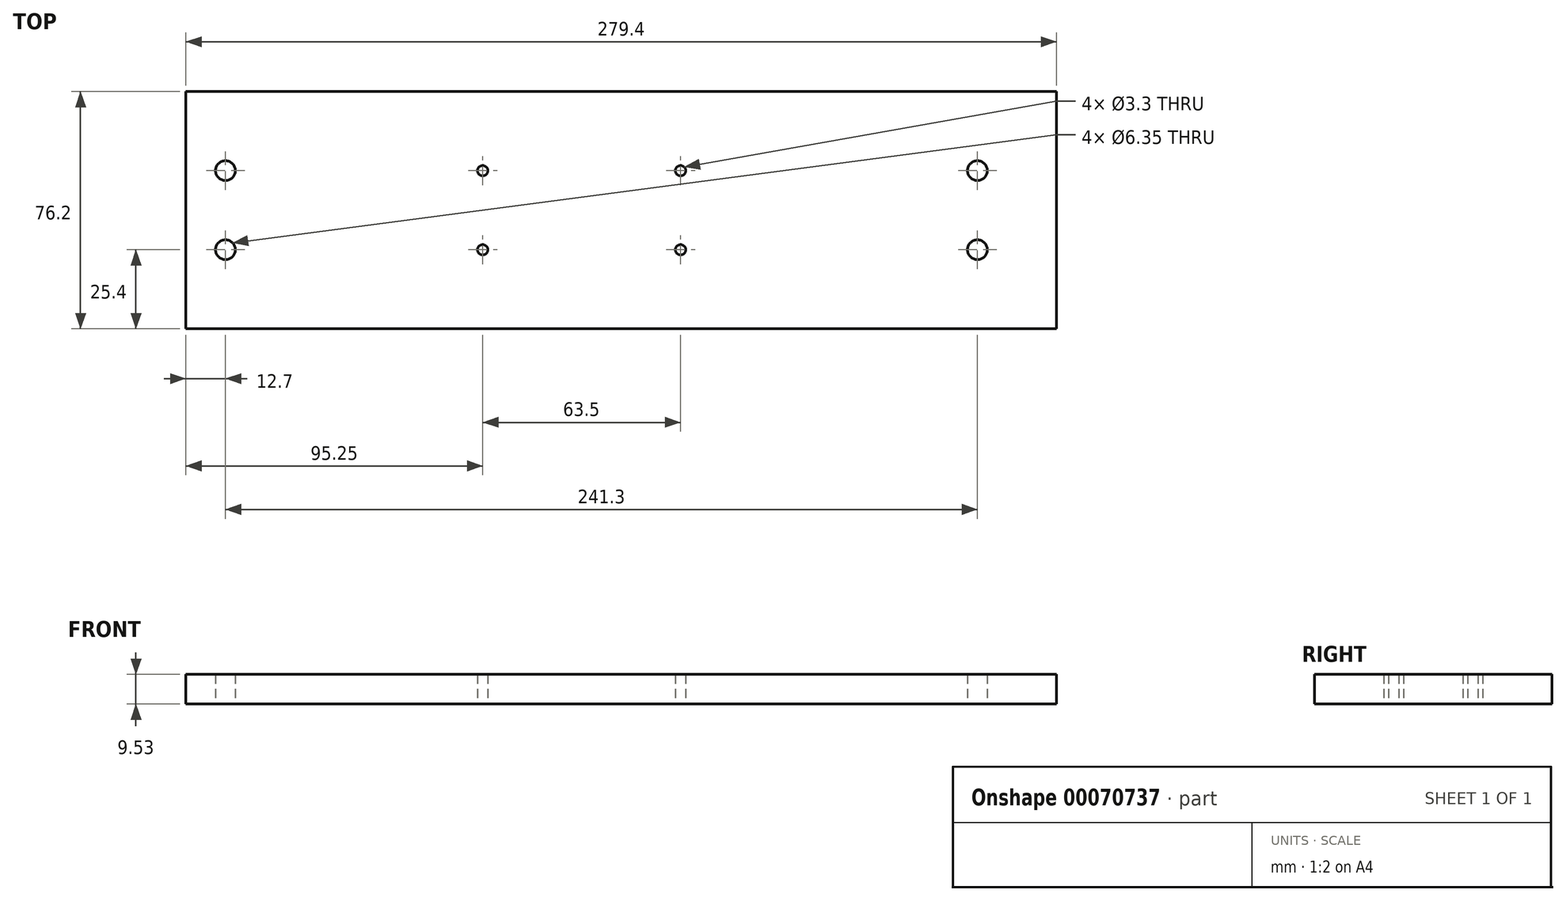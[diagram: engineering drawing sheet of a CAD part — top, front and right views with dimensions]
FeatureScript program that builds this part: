
annotation { "Feature Type Name" : "Feature", "Feature Type Description" : "" }
export const myFeature = defineFeature(function(context is Context, id is Id, definition is map)
    precondition{}
    {
        {
            var Q0;
            Q0=qCreatedBy(makeId("Top.planeOp"),FACE);
            var sketch = newSketch(context, id + "F0", { "sketchPlane" : qUnion([Q0])});
            skLineSegment(sketch, "E0.bottom", {"start": v(0, 0) * mm, "end": v(279.4, 0) * mm});
            skLineSegment(sketch, "E0.top", {"start": v(0, 76.2) * mm, "end": v(279.4, 76.2) * mm});
            skLineSegment(sketch, "E0.left", {"start": v(0, 0) * mm, "end": v(0, 76.2) * mm});
            skLineSegment(sketch, "E0.right", {"start": v(279.4, 0) * mm, "end": v(279.4, 76.2) * mm});
            skLineSegment(sketch, "E1", {"start": v(-31.93, 38.1) * mm, "end": v(355.88, 38.1) * mm});
            skPoint(sketch, "E1.startSnap0", {"position": v(0, 38.1) * mm});
            skCircle(sketch, "E2", {"center": v(12.7, 50.8) * mm, "radius": 3.18 * mm});
            skCircle(sketch, "E3", {"center": v(12.7, 25.4) * mm, "radius": 3.18 * mm});
            skCircle(sketch, "E4", {"center": v(95.25, 50.8) * mm, "radius": 1.65 * mm});
            skCircle(sketch, "E5", {"center": v(95.25, 25.4) * mm, "radius": 1.65 * mm});
            skCircle(sketch, "E6", {"center": v(158.75, 25.4) * mm, "radius": 1.65 * mm});
            skCircle(sketch, "E7", {"center": v(158.75, 50.8) * mm, "radius": 1.65 * mm});
            skCircle(sketch, "E8", {"center": v(254, 50.8) * mm, "radius": 3.18 * mm});
            skCircle(sketch, "E9", {"center": v(254, 25.4) * mm, "radius": 3.18 * mm});
            skSolve(sketch);
        }
        {
            var Q0;
            {var subQ5=sQuery(id+"F0.wireOp",EDGE,"E0.top");Q0=makeQuery(id+"F0.imprint","IMPRINT",FACE,{"disambiguationData":[TD([[makeQuery(id+"F0.imprint","IMPRINT",EDGE,{"derivedFrom":subQ5}),-1.0]])]});}
            var Q1;
            {var subQ5=sQuery(id+"F0.wireOp",EDGE,"E0.bottom");Q1=makeQuery(id+"F0.imprint","IMPRINT",FACE,{"disambiguationData":[TD([[makeQuery(id+"F0.imprint","IMPRINT",EDGE,{"derivedFrom":subQ5}),1.0]])]});}
            extrude(context, id + "F1", {"entities" : qUnion([Q0, Q1]), "depth" : 9.52 * mm});
        }
    });
